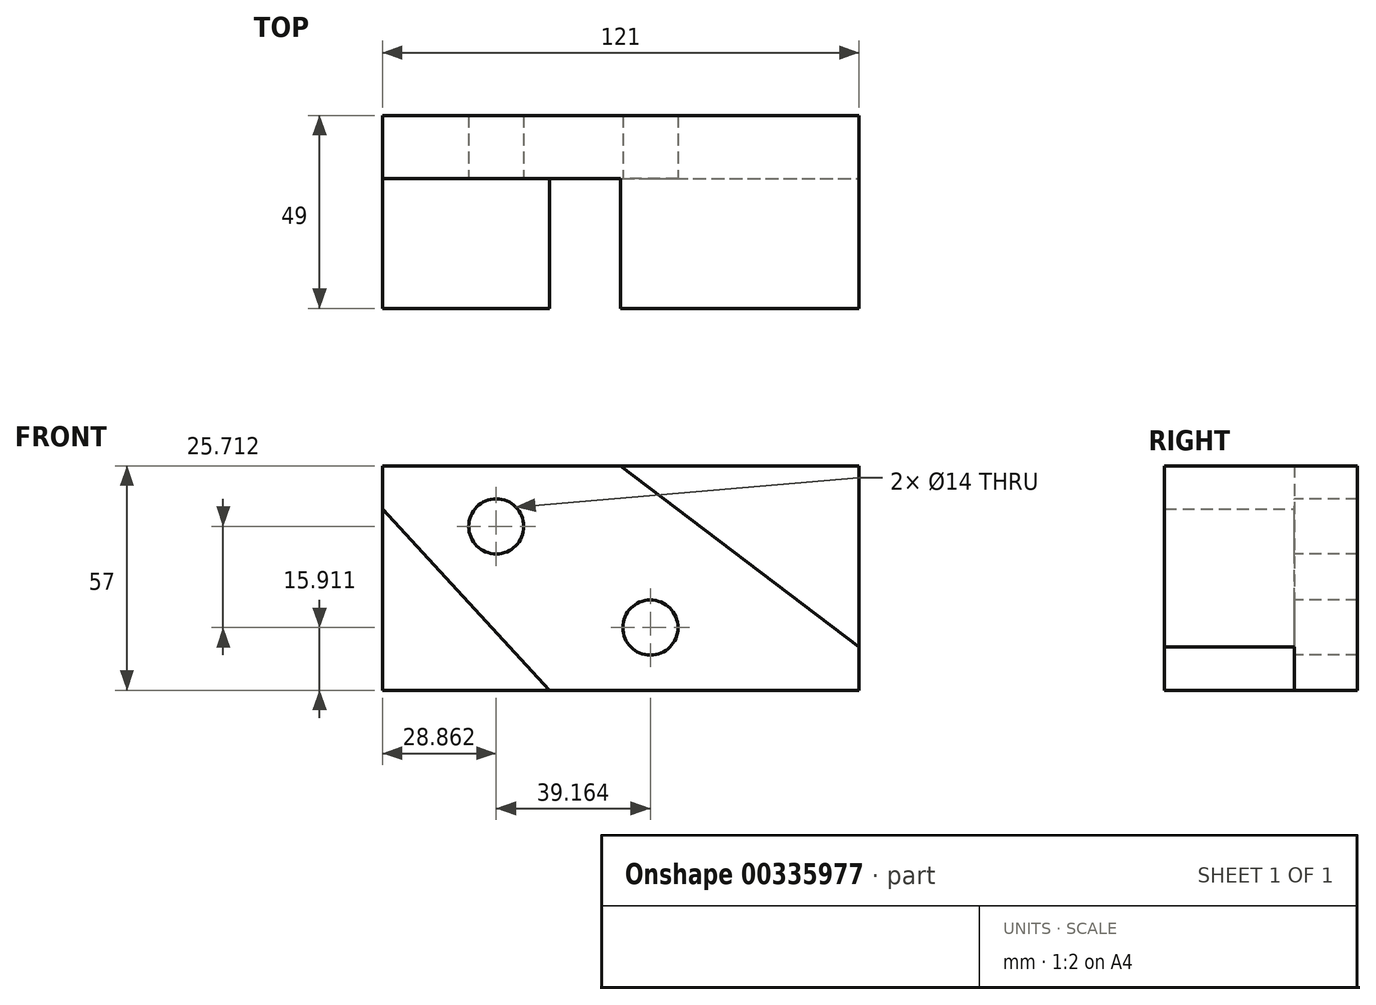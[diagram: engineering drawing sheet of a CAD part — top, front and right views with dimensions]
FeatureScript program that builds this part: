
annotation { "Feature Type Name" : "Feature", "Feature Type Description" : "" }
export const myFeature = defineFeature(function(context is Context, id is Id, definition is map)
    precondition{}
    {
        {
            var Q0;
            Q0=qCreatedBy(makeId("Top.planeOp"),FACE);
            var sketch = newSketch(context, id + "F0", { "sketchPlane" : qUnion([Q0])});
            skLineSegment(sketch, "E0.bottom", {"start": v(0, 0) * mm, "end": v(121, 0) * mm});
            skLineSegment(sketch, "E0.top", {"start": v(0, 16) * mm, "end": v(121, 16) * mm});
            skLineSegment(sketch, "E0.left", {"start": v(0, 0) * mm, "end": v(0, 16) * mm});
            skLineSegment(sketch, "E0.right", {"start": v(121, 0) * mm, "end": v(121, 16) * mm});
            skSolve(sketch);
        }
        {
            var Q0;
            Q0 = qSketchRegion(id + "F0", true);
            extrude(context, id + "F1", {"entities" : qUnion([Q0]), "depth" : 57 * mm});
        }
        {
            var Q0;
            Q0=makeQuery(id+"F1.opExtrude","SWEPT_FACE",FACE,{"disambiguationData":[OSD([sQuery(id+"F0.wireOp",EDGE,"E0.bottom")])]});
            var sketch = newSketch(context, id + "F2", { "sketchPlane" : qUnion([Q0])});
            skLineSegment(sketch, "E1", {"start": v(0, 46) * mm, "end": v(0, 0) * mm});
            skLineSegment(sketch, "E2", {"start": v(0, 0) * mm, "end": v(42.4, 0) * mm});
            skLineSegment(sketch, "E3", {"start": v(42.4, 0) * mm, "end": v(0, 46) * mm});
            skLineSegment(sketch, "E4", {"start": v(18.8, 25.62) * mm, "end": v(18.8, 0) * mm});
            skSolve(sketch);
        }
        {
            var Q0;
            Q0 = qSketchRegion(id + "F2", true);
            extrude(context, id + "F3", {"entities" : qUnion([Q0]), "operationType" : NewBodyOperationType.ADD, "depth" : 33 * mm});
        }
        {
            var Q0;
            Q0=makeQuery(id+"F1.opExtrude","SWEPT_FACE",FACE,{"disambiguationData":[OSD([sQuery(id+"F0.wireOp",EDGE,"E0.bottom")])]});
            var sketch = newSketch(context, id + "F4", { "sketchPlane" : qUnion([Q0])});
            skLineSegment(sketch, "E5", {"start": v(121, 57) * mm, "end": v(60.5, 57) * mm});
            skLineSegment(sketch, "E6", {"start": v(60.5, 57) * mm, "end": v(121, 11) * mm});
            skLineSegment(sketch, "E7", {"start": v(121, 11) * mm, "end": v(121, 57) * mm});
            skSolve(sketch);
        }
        {
            var Q0;
            Q0 = qSketchRegion(id + "F4", true);
            extrude(context, id + "F5", {"entities" : qUnion([Q0]), "operationType" : NewBodyOperationType.ADD, "depth" : 33 * mm});
        }
        {
            var Q0;
            Q0=makeQuery(id+"F1.opExtrude","SWEPT_FACE",FACE,{"disambiguationData":[OSD([sQuery(id+"F0.wireOp",EDGE,"E0.bottom")])]});
            var sketch = newSketch(context, id + "F6", { "sketchPlane" : qUnion([Q0])});
            skCircle(sketch, "E8", {"center": v(28.86, 41.62) * mm, "radius": 7 * mm});
            skCircle(sketch, "E9", {"center": v(68.03, 15.91) * mm, "radius": 7 * mm});
            skSolve(sketch);
        }
        {
            var Q0;
            Q0 = qSketchRegion(id + "F6", true);
            extrude(context, id + "F7", {"entities" : qUnion([Q0]), "operationType" : NewBodyOperationType.REMOVE, "endBound" : BoundingType.THROUGH_ALL, "oppositeDirection" : true, "depth" : 25 * mm});
        }
    });
